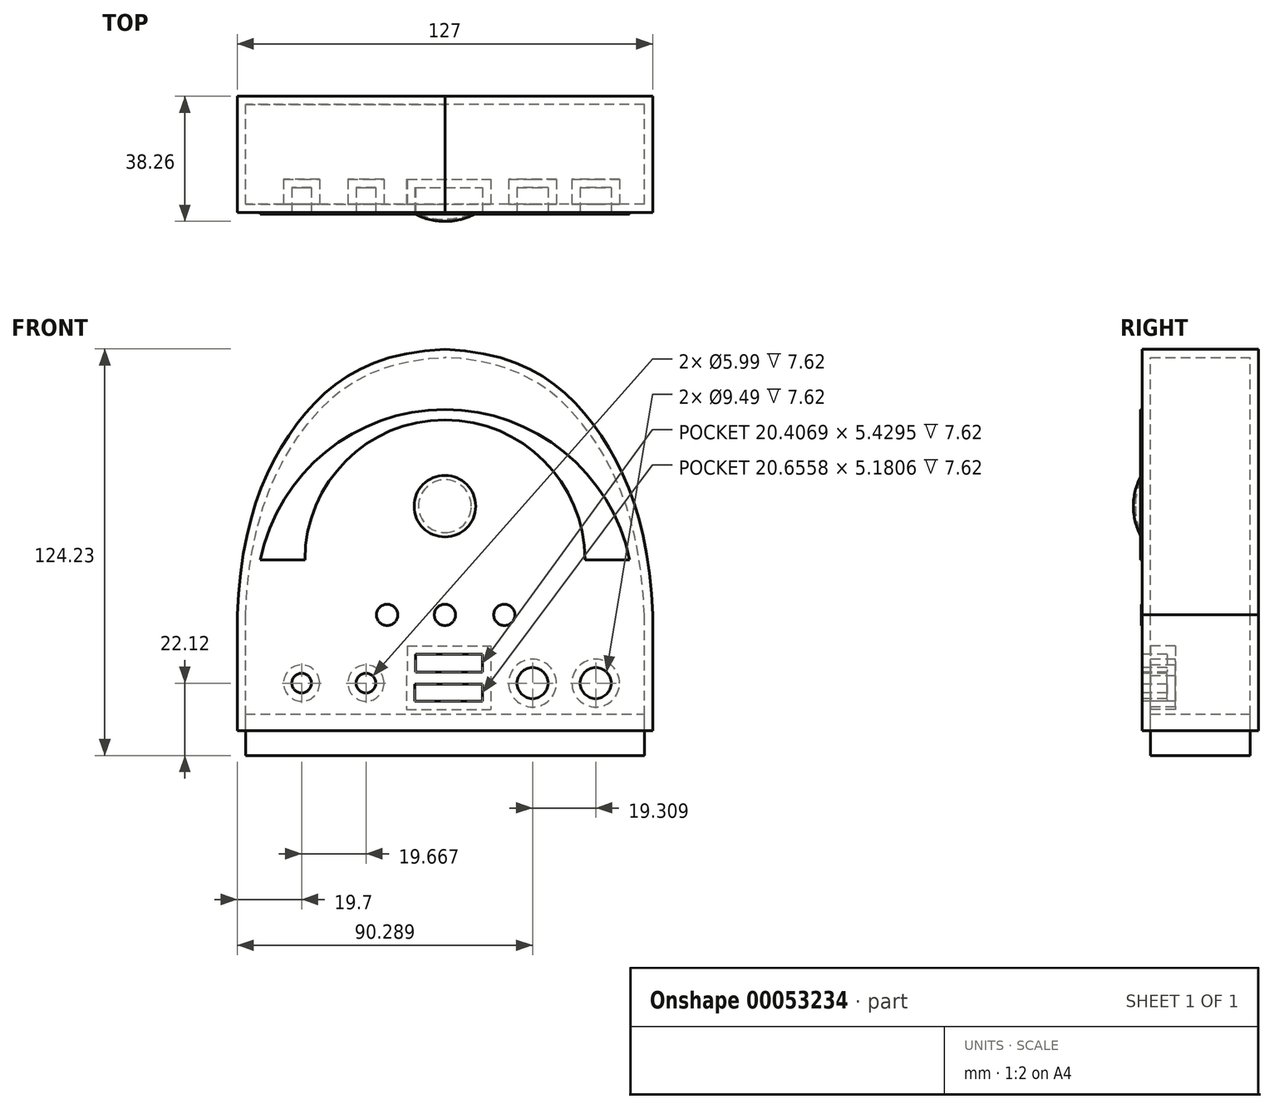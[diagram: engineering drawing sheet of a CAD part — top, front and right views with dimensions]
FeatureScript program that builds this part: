
annotation { "Feature Type Name" : "Feature", "Feature Type Description" : "" }
export const myFeature = defineFeature(function(context is Context, id is Id, definition is map)
    precondition{}
    {
        {
            var Q0;
            Q0=qCreatedBy(makeId("Front.planeOp"),FACE);
            var sketch = newSketch(context, id + "F0", { "sketchPlane" : qUnion([Q0])});
            skLineSegment(sketch, "E0", {"start": v(0, -52.16) * mm, "end": v(63.5, -52.16) * mm});
            skLineSegment(sketch, "E1", {"start": v(63.5, -52.16) * mm, "end": v(63.5, -16.8) * mm});
            skFitSpline(sketch, "E2", {"points": [v(63.5, -16.8) * mm, v(45.09, 41.7) * mm, v(0, 64.45) * mm], "startDerivative": vector(-6.09, 155.18) * mm, "endDerivative": vector(-147.99, 7.08) * mm});
            skFitSpline(sketch, "E3.MirrorCS", {"points": [v(-63.5, -16.8) * mm, v(-45.09, 41.7) * mm, v(0, 64.45) * mm], "startDerivative": vector(6.09, 155.18) * mm, "endDerivative": vector(147.99, 7.08) * mm});
            skLineSegment(sketch, "E4.MirrorCS", {"start": v(-63.5, -52.16) * mm, "end": v(-63.5, -16.8) * mm});
            skLineSegment(sketch, "E5.MirrorCS", {"start": v(0, -52.16) * mm, "end": v(-63.5, -52.16) * mm});
            skSolve(sketch);
        }
        {
            var Q0;
            Q0 = qSketchRegion(id + "F0", true);
            extrude(context, id + "F1", {"entities" : qUnion([Q0]), "depth" : 35.56 * mm});
        }
        {
            var Q0;
            Q0=makeQuery(id+"F1.opExtrude","CAP_FACE",FACE,{"disambiguationData":[OSD([sQuery(id+"F0.wireOp",EDGE,"E0"),sQuery(id+"F0.wireOp",EDGE,"E1"),sQuery(id+"F0.wireOp",EDGE,"E2"),sQuery(id+"F0.wireOp",EDGE,"E3.MirrorCS"),sQuery(id+"F0.wireOp",EDGE,"E4.MirrorCS"),sQuery(id+"F0.wireOp",EDGE,"E5.MirrorCS")])],"isStart":false});
            var sketch = newSketch(context, id + "F2", { "sketchPlane" : qUnion([Q0])});
            skLineSegment(sketch, "E6.bottom", {"start": v(-8.96, -28.87) * mm, "end": v(11.45, -28.87) * mm});
            skLineSegment(sketch, "E6.top", {"start": v(-8.96, -34.3) * mm, "end": v(11.45, -34.3) * mm});
            skLineSegment(sketch, "E6.left", {"start": v(-8.96, -28.87) * mm, "end": v(-8.96, -34.3) * mm});
            skLineSegment(sketch, "E6.right", {"start": v(11.45, -28.87) * mm, "end": v(11.45, -34.3) * mm});
            skLineSegment(sketch, "E7.bottom", {"start": v(-9.2, -38.04) * mm, "end": v(11.45, -38.04) * mm});
            skLineSegment(sketch, "E7.top", {"start": v(-9.2, -43.22) * mm, "end": v(11.45, -43.22) * mm});
            skLineSegment(sketch, "E7.left", {"start": v(-9.2, -38.04) * mm, "end": v(-9.2, -43.22) * mm});
            skLineSegment(sketch, "E7.right", {"start": v(11.45, -38.04) * mm, "end": v(11.45, -43.22) * mm});
            skCircle(sketch, "E8", {"center": v(26.79, -37.66) * mm, "radius": 4.75 * mm});
            skCircle(sketch, "E9", {"center": v(46.1, -37.66) * mm, "radius": 4.75 * mm});
            skCircle(sketch, "E10", {"center": v(-24.13, -37.66) * mm, "radius": 3 * mm});
            skCircle(sketch, "E11", {"center": v(-43.8, -37.66) * mm, "radius": 3 * mm});
            skSolve(sketch);
        }
        {
            var Q0;
            Q0 = qSketchRegion(id + "F2", true);
            extrude(context, id + "F3", {"entities" : qUnion([Q0]), "operationType" : NewBodyOperationType.REMOVE, "oppositeDirection" : true, "depth" : 7.62 * mm});
        }
        {
            var Q0;
            Q0=makeQuery(id+"F1.opExtrude","CAP_FACE",FACE,{"disambiguationData":[OSD([sQuery(id+"F0.wireOp",EDGE,"E0"),sQuery(id+"F0.wireOp",EDGE,"E1"),sQuery(id+"F0.wireOp",EDGE,"E2"),sQuery(id+"F0.wireOp",EDGE,"E3.MirrorCS"),sQuery(id+"F0.wireOp",EDGE,"E4.MirrorCS"),sQuery(id+"F0.wireOp",EDGE,"E5.MirrorCS")])],"isStart":false});
            var sketch = newSketch(context, id + "F4", { "sketchPlane" : qUnion([Q0])});
            skArc(sketch, "E12", {"start": v(-42.8, 0) * mm, "mid": v(0, 42.8) * mm, "end": v(42.8, 0) * mm});
            skArc(sketch, "E13", {"start": v(-56.5, 0) * mm, "mid": v(0, 45.95) * mm, "end": v(56.5, 0) * mm});
            skLineSegment(sketch, "E14", {"start": v(-42.8, 0) * mm, "end": v(-56.5, 0) * mm});
            skLineSegment(sketch, "E15", {"start": v(42.8, 0) * mm, "end": v(56.5, 0) * mm});
            skCircle(sketch, "E16", {"center": v(-17.67, -16.8) * mm, "radius": 3.24 * mm});
            skCircle(sketch, "E17", {"center": v(0, -16.8) * mm, "radius": 3.24 * mm});
            skCircle(sketch, "E18", {"center": v(18.17, -16.8) * mm, "radius": 3.24 * mm});
            skSolve(sketch);
        }
        {
            var Q0;
            Q0 = qSketchRegion(id + "F4", true);
            extrude(context, id + "F5", {"entities" : qUnion([Q0]), "depth" : 0.25 * mm});
        }
        {
            var Q0;
            Q0=makeQuery(id+"F5.opExtrude","CAP_FACE",FACE,{"disambiguationData":[OSD([sQuery(id+"F4.wireOp",EDGE,"E12"),sQuery(id+"F4.wireOp",EDGE,"E13"),sQuery(id+"F4.wireOp",EDGE,"E14"),sQuery(id+"F4.wireOp",EDGE,"E15")])],"isStart":false});
            extrude(context, id + "F6", {"entities" : qUnion([Q0]), "depth" : 0.25 * mm});
        }
        {
            var Q0;
            Q0=makeQuery(id+"F1.opExtrude","SWEPT_FACE",FACE,{"disambiguationData":[OSD([sQuery(id+"F0.wireOp",EDGE,"E0"),sQuery(id+"F0.wireOp",EDGE,"E5.MirrorCS")])]});
            shell(context, id + "F7", {"entities" : qUnion([Q0]), "thickness" : 2.54 * mm});
        }
        {
            var Q0;
            Q0=makeQuery(id+"F1.opExtrude","SWEPT_FACE",FACE,{"disambiguationData":[OSD([sQuery(id+"F0.wireOp",EDGE,"E0"),sQuery(id+"F0.wireOp",EDGE,"E5.MirrorCS")])]});
            cPlane(context, id + "F8", {"entities" : qUnion([Q0]), "cplaneType" : CPlaneType.OFFSET, "offset" : 5.08 * mm, "oppositeDirection" : true, "width" : 152.4 * mm, "height" : 152.4 * mm});
        }
        {
            var Q0;
            Q0=qCreatedBy(id+"F8.planeOp",FACE);
            var sketch = newSketch(context, id + "F9", { "sketchPlane" : qUnion([Q0])});
            skLineSegment(sketch, "E19.bottom", {"start": v(-60.96, 33.02) * mm, "end": v(60.96, 33.02) * mm});
            skLineSegment(sketch, "E19.top", {"start": v(-60.96, 2.54) * mm, "end": v(60.96, 2.54) * mm});
            skLineSegment(sketch, "E19.left", {"start": v(-60.96, 33.02) * mm, "end": v(-60.96, 2.54) * mm});
            skLineSegment(sketch, "E19.right", {"start": v(60.96, 33.02) * mm, "end": v(60.96, 2.54) * mm});
            skSolve(sketch);
        }
        {
            var Q0;
            Q0 = qSketchRegion(id + "F9", true);
            extrude(context, id + "F10", {"entities" : qUnion([Q0]), "depth" : 12.7 * mm});
        }
        {
            var Q0;
            Q0=qCreatedBy(id+"F8.planeOp",FACE);
            cPlane(context, id + "F11", {"entities" : qUnion([Q0]), "cplaneType" : CPlaneType.OFFSET, "offset" : 63.5 * mm, "oppositeDirection" : true, "width" : 152.4 * mm, "height" : 152.4 * mm});
        }
        {
            var Q0;
            Q0=qCreatedBy(id+"F11.planeOp",FACE);
            var sketch = newSketch(context, id + "F12", { "sketchPlane" : qUnion([Q0])});
            skArc(sketch, "E20", {"start": v(0, 38.26) * mm, "mid": v(4.86, 37.65) * mm, "end": v(9.41, 35.85) * mm});
            skArc(sketch, "E21", {"start": v(0, 37.65) * mm, "mid": v(4.14, 37.2) * mm, "end": v(8.07, 35.85) * mm});
            skLineSegment(sketch, "E22", {"start": v(0, 38.26) * mm, "end": v(0, 37.65) * mm});
            skLineSegment(sketch, "E23", {"start": v(8.07, 35.85) * mm, "end": v(9.41, 35.85) * mm});
            skLineSegment(sketch, "E24", {"start": v(0, 43.94) * mm, "end": v(0, 27.73) * mm, "construction": true});
            skSolve(sketch);
        }
        {
            var Q0;
            Q0 = qSketchRegion(id + "F12", true);
            var Q1;
            Q1=sQuery(id+"F12.wireOp",EDGE,"E24");
            revolve(context, id + "F13", {"entities" : qUnion([Q0]), "axis" : qUnion([Q1]), "revolveType" : RevolveType.FULL});
        }
    });
